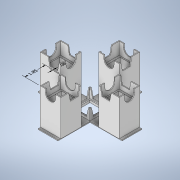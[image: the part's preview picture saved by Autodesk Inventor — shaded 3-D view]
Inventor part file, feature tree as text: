
AUTODESK INVENTOR PART (.ipt)
format: ipt  version: 2021 (Build 250183000, 183)  size: 451,072 bytes
history: native  units: in
note: dims shown in document units (in); Inventor stores cm internally (conversion verified against a paired STEP export)
features: move_body x32, direct_edit x7, other x3, sketch x1, imported_body x1
ambient origin geometry x8: Origin, YZ Plane, XZ Plane, XY Plane, X Axis, Y Axis, Z Axis, Center Point
bodies: Solid1 (feature_tree)
feature tree (44):
  other  "Annotations"
  sketch  "Sketch1"  dims[d6=0.0in d7=0.0in d8=0.5709in d9=0.0in d10=0.0in d11=0.5709in d12=0.0in d13=0.0in d14=0.5709in d15=0.0in d16=0.0in d17=0.5709in d18=0.0in d19=0.0in d20=0.5709in d21=0.0in d22=0.0in d23=0.5709in d24=0.0in d25=0.0in d26=0.5709in d27=0.0in d28=0.0in d29=0.5709in d30=0.0in d31=0.0in d32=-0.5709in d33=0.0in d34=0.0in d35=-0.5709in d36=0.0in d37=0.0in d38=-0.5709in d39=0.0in d40=0.0in d41=-0.5709in d42=0.0in d43=0.0in d44=-0.5709in d45=0.0in d46=0.0in d47=-0.5709in d48=0.0in d49=0.0in d50=-0.5709in d51=0.0in d52=0.0in d53=-0.5709in d57=0.0in d58=0.0in d59=0.0709in d60=0.0in d61=0.0in d62=0.0709in d63=0.0in d64=0.0in d65=0.0709in d66=0.0in d67=0.0in d68=0.0709in d69=0.0in d70=0.0in d71=0.0709in d72=0.0in d73=0.0in d74=0.0709in d75=0.0in d76=0.0in d77=0.0709in d78=0.0in d79=0.0in d80=0.0709in d81=0.0in d82=0.0in d83=-0.0709in d84=0.0in d85=0.0in d86=-0.0709in d87=0.0in d88=0.0in d89=-0.0709in d90=0.0in d91=0.0in d92=-0.0709in d93=0.0in d94=0.0in d95=-0.0709in d96=0.0in d97=0.0in d98=-0.0709in d99=0.0in d100=0.0in d101=-0.0709in d102=0.0in d103=0.0in d104=-0.0709in d0=0.2807in d1=0.3127in d2=0.0787in d3=0.2723in d4=0.1116in d5=1.8504in]
  direct_edit  "Direct Edit1"
  direct_edit  "Direct Edit2"
  direct_edit  "Direct Edit3"
  direct_edit  "Direct Edit4"
  direct_edit  "Direct Edit5"
  direct_edit  "Direct Edit6"
  direct_edit  "Direct Edit7"
  imported_body  "Base1"
  move_body  "Move1"
  move_body  "Move2"
  move_body  "Move3"
  move_body  "Move4"
  move_body  "Move5"
  move_body  "Move6"
  move_body  "Move7"
  move_body  "Move8"
  move_body  "Move9"
  move_body  "Move10"
  move_body  "Move11"
  move_body  "Move12"
  move_body  "Move13"
  move_body  "Move14"
  move_body  "Move15"
  move_body  "Move16"
  move_body  "Move17"
  move_body  "Move18"
  move_body  "Move19"
  move_body  "Move20"
  move_body  "Move21"
  move_body  "Move22"
  move_body  "Move23"
  move_body  "Move24"
  move_body  "Move25"
  move_body  "Move26"
  move_body  "Move27"
  move_body  "Move28"
  move_body  "Move29"
  move_body  "Move30"
  move_body  "Move31"
  move_body  "Move32"
  other  "Linear Dimension 1"
  other  "Linear Dimension 2"
